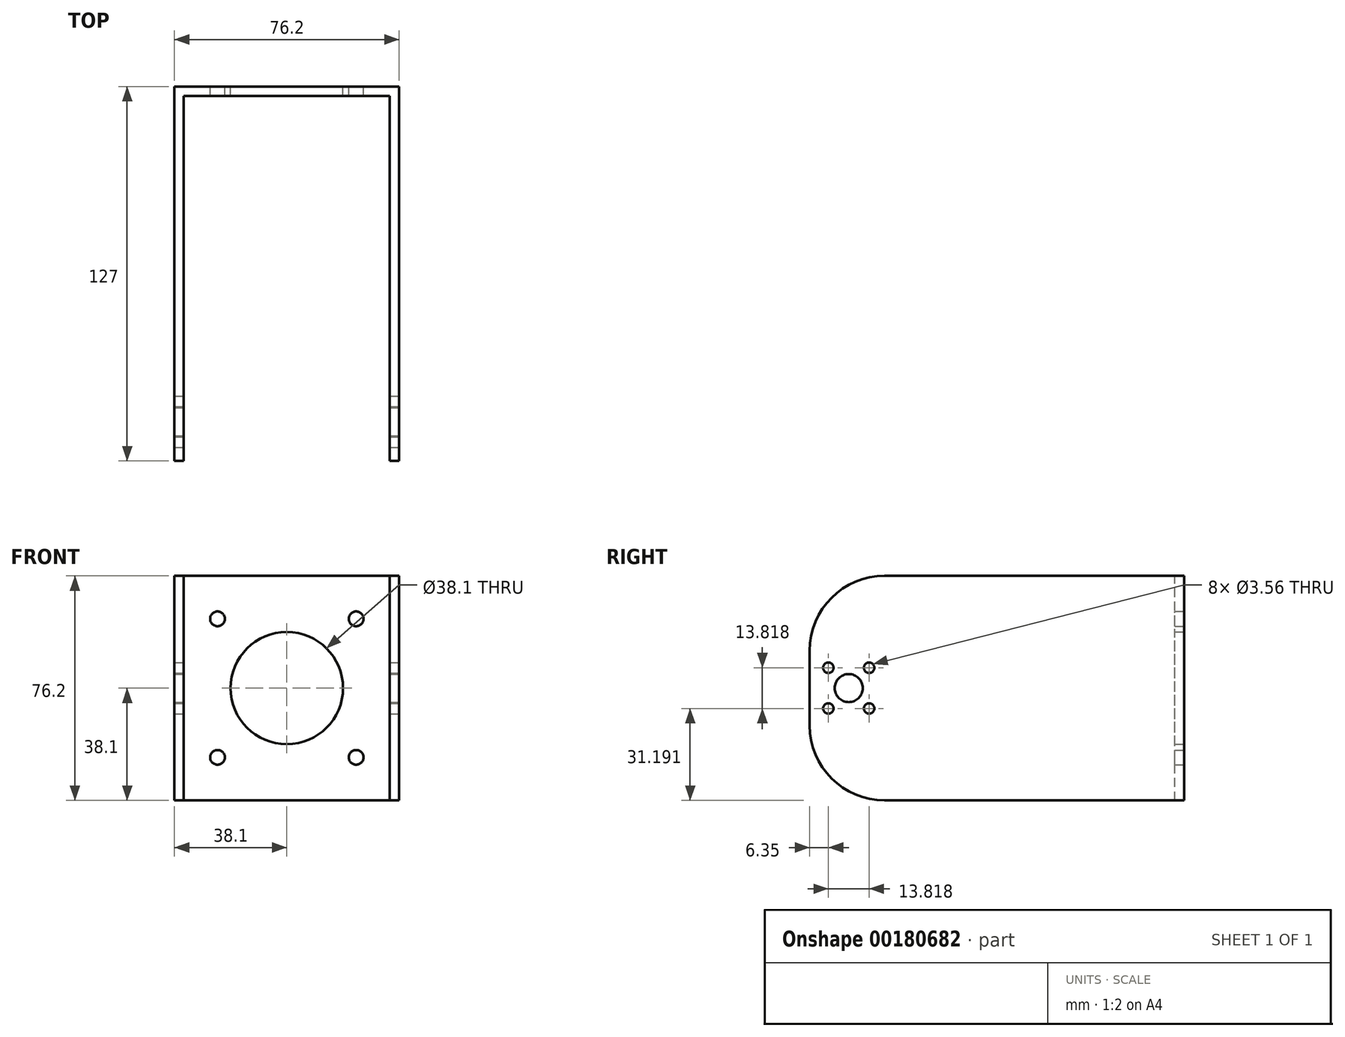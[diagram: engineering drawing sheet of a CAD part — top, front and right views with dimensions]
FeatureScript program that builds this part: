
annotation { "Feature Type Name" : "Feature", "Feature Type Description" : "" }
export const myFeature = defineFeature(function(context is Context, id is Id, definition is map)
    precondition{}
    {
        {
            var Q0;
            Q0=qCreatedBy(makeId("Front.planeOp"),FACE);
            var sketch = newSketch(context, id + "F0", { "sketchPlane" : qUnion([Q0])});
            skLineSegment(sketch, "E0.bottom", {"start": v(38.1, -38.1) * mm, "end": v(-38.1, -38.1) * mm});
            skLineSegment(sketch, "E0.top", {"start": v(38.1, 38.1) * mm, "end": v(-38.1, 38.1) * mm});
            skLineSegment(sketch, "E0.left", {"start": v(38.1, -38.1) * mm, "end": v(38.1, 38.1) * mm});
            skLineSegment(sketch, "E0.right", {"start": v(-38.1, -38.1) * mm, "end": v(-38.1, 38.1) * mm});
            skPoint(sketch, "E0.middle", {"position": v(0, 0) * mm});
            skLineSegment(sketch, "E1", {"start": v(-34.93, 38.1) * mm, "end": v(-34.93, -38.1) * mm});
            skLineSegment(sketch, "E2", {"start": v(-34.92, -38.1) * mm, "end": v(34.92, -38.1) * mm});
            skLineSegment(sketch, "E3", {"start": v(34.92, -38.1) * mm, "end": v(34.92, 38.1) * mm});
            skCircle(sketch, "E4", {"center": v(0, 0) * mm, "radius": 19.05 * mm});
            skCircle(sketch, "E5", {"center": v(-23.5, 23.5) * mm, "radius": 2.5 * mm});
            skCircle(sketch, "E6.0.1.0", {"center": v(-23.5, -23.5) * mm, "radius": 2.5 * mm});
            skCircle(sketch, "E6.1.0.0", {"center": v(23.5, 23.5) * mm, "radius": 2.5 * mm});
            skCircle(sketch, "E6.1.1.0", {"center": v(23.5, -23.5) * mm, "radius": 2.5 * mm});
            skLineSegment(sketch, "E6.direction1", {"start": v(-23.5, 23.5) * mm, "end": v(23.5, 23.5) * mm, "construction": true});
            skLineSegment(sketch, "E6.direction2", {"start": v(-23.5, 23.5) * mm, "end": v(-23.5, -23.5) * mm, "construction": true});
            skSolve(sketch);
        }
        {
            var Q0;
            {var subQ1=sQuery(id+"F0.wireOp",EDGE,"E1");Q0=makeQuery(id+"F0.imprint","IMPRINT",FACE,{"disambiguationData":[TD([[makeQuery(id+"F0.imprint","IMPRINT",EDGE,{"derivedFrom":subQ1}),1.0]])]});}
            extrude(context, id + "F1", {"entities" : qUnion([Q0]), "depth" : 3.17 * mm});
        }
        {
            var Q0;
            {var subQ0=sQuery(id+"F0.wireOp",EDGE,"E0.right");Q0=makeQuery(id+"F0.imprint","IMPRINT",FACE,{"disambiguationData":[TD([[makeQuery(id+"F0.imprint","IMPRINT",EDGE,{"derivedFrom":subQ0}),-1.0]])]});}
            var Q1;
            {var subQ0=sQuery(id+"F0.wireOp",EDGE,"E0.left");Q1=makeQuery(id+"F0.imprint","IMPRINT",FACE,{"disambiguationData":[TD([[makeQuery(id+"F0.imprint","IMPRINT",EDGE,{"derivedFrom":subQ0}),1.0]])]});}
            extrude(context, id + "F2", {"entities" : qUnion([Q0, Q1]), "operationType" : NewBodyOperationType.ADD, "depth" : 127 * mm});
        }
        {
            var Q0;
            Q0=makeQuery(id+"F2.opExtrude","SWEPT_FACE",FACE,{"disambiguationData":[OSD([sQuery(id+"F0.wireOp",EDGE,"E0.left")])]});
            var sketch = newSketch(context, id + "F3", { "sketchPlane" : qUnion([Q0])});
            skCircle(sketch, "E7", {"center": v(-113.74, 0) * mm, "radius": 4.76 * mm});
            skCircle(sketch, "E8", {"center": v(-120.65, 6.9) * mm, "radius": 1.78 * mm});
            skCircle(sketch, "E9.0.1.0", {"center": v(-120.65, -6.9) * mm, "radius": 1.78 * mm});
            skCircle(sketch, "E9.1.0.0", {"center": v(-106.83, 6.9) * mm, "radius": 1.78 * mm});
            skCircle(sketch, "E9.1.1.0", {"center": v(-106.83, -6.9) * mm, "radius": 1.78 * mm});
            skLineSegment(sketch, "E9.direction1", {"start": v(-120.65, 6.9) * mm, "end": v(-106.83, 6.9) * mm, "construction": true});
            skLineSegment(sketch, "E9.direction2", {"start": v(-120.65, 6.9) * mm, "end": v(-120.65, -6.9) * mm, "construction": true});
            skSolve(sketch);
        }
        {
            var Q0;
            Q0=makeQuery(id+"F3.imprint","IMPRINT",FACE,{"disambiguationData":[TD([[makeQuery(id+"F3.imprint","IMPRINT",EDGE,{"derivedFrom":sQuery(id+"F3.wireOp",EDGE,"E8")}),1.0]])]});
            var Q1;
            Q1=makeQuery(id+"F3.imprint","IMPRINT",FACE,{"disambiguationData":[TD([[makeQuery(id+"F3.imprint","IMPRINT",EDGE,{"derivedFrom":sQuery(id+"F3.wireOp",EDGE,"E9.1.0.0")}),1.0]])]});
            var Q2;
            Q2=makeQuery(id+"F3.imprint","IMPRINT",FACE,{"disambiguationData":[TD([[makeQuery(id+"F3.imprint","IMPRINT",EDGE,{"derivedFrom":sQuery(id+"F3.wireOp",EDGE,"E9.1.1.0")}),1.0]])]});
            var Q3;
            Q3=makeQuery(id+"F3.imprint","IMPRINT",FACE,{"disambiguationData":[TD([[makeQuery(id+"F3.imprint","IMPRINT",EDGE,{"derivedFrom":sQuery(id+"F3.wireOp",EDGE,"E9.0.1.0")}),1.0]])]});
            var Q4;
            Q4=makeQuery(id+"F3.imprint","IMPRINT",FACE,{"disambiguationData":[TD([[makeQuery(id+"F3.imprint","IMPRINT",EDGE,{"derivedFrom":sQuery(id+"F3.wireOp",EDGE,"E7")}),1.0]])]});
            extrude(context, id + "F4", {"entities" : qUnion([Q0, Q1, Q2, Q3, Q4]), "operationType" : NewBodyOperationType.REMOVE, "endBound" : BoundingType.THROUGH_ALL, "oppositeDirection" : true, "depth" : 25.4 * mm});
        }
        {
            var Q0;
            {var subQ0=sQuery(id+"F0.wireOp",EDGE,"E0.top");Q0=makeQuery(id+"F2.opExtrude","CAP_EDGE",EDGE,{"disambiguationData":[OSD([subQ0]),TDD([makeQuery(id+"F0.imprint","IMPRINT",EDGE,{"disambiguationData":[TD([[makeQuery(id+"F0.imprint","INTERSECT",VERTEX,{"derivedFrom":[subQ0,sQuery(id+"F0.wireOp",EDGE,"E0.left")]}),-1.0]])],"derivedFrom":subQ0})])],"isStart":false});}
            fillet(context, id + "F5", {"entities" : qUnion([Q0]), "radius" : 25.4 * mm, "tangentPropagation" : true, "allowEdgeOverflow" : false});
        }
        {
            var Q0;
            {var subQ0=sQuery(id+"F0.wireOp",EDGE,"E0.top");Q0=makeQuery(id+"F2.opExtrude","CAP_EDGE",EDGE,{"disambiguationData":[OSD([subQ0]),TDD([makeQuery(id+"F0.imprint","IMPRINT",EDGE,{"disambiguationData":[TD([[makeQuery(id+"F0.imprint","INTERSECT",VERTEX,{"derivedFrom":[subQ0,sQuery(id+"F0.wireOp",EDGE,"E0.right")]}),1.0]])],"derivedFrom":subQ0})])],"isStart":false});}
            fillet(context, id + "F6", {"entities" : qUnion([Q0]), "radius" : 25.4 * mm, "tangentPropagation" : true, "allowEdgeOverflow" : false});
        }
        {
            var Q0;
            {var subQ0=sQuery(id+"F0.wireOp",EDGE,"E0.bottom");Q0=makeQuery(id+"F2.opExtrude","CAP_EDGE",EDGE,{"disambiguationData":[OSD([subQ0]),TDD([makeQuery(id+"F0.imprint","IMPRINT",EDGE,{"disambiguationData":[TD([[makeQuery(id+"F0.imprint","INTERSECT",VERTEX,{"derivedFrom":[subQ0,sQuery(id+"F0.wireOp",EDGE,"E0.right")]}),1.0]])],"derivedFrom":subQ0})])],"isStart":false});}
            fillet(context, id + "F7", {"entities" : qUnion([Q0]), "radius" : 25.4 * mm, "tangentPropagation" : true, "allowEdgeOverflow" : false});
        }
        {
            var Q0;
            {var subQ0=sQuery(id+"F0.wireOp",EDGE,"E0.bottom");Q0=makeQuery(id+"F2.opExtrude","CAP_EDGE",EDGE,{"disambiguationData":[OSD([subQ0]),TDD([makeQuery(id+"F0.imprint","IMPRINT",EDGE,{"disambiguationData":[TD([[makeQuery(id+"F0.imprint","INTERSECT",VERTEX,{"derivedFrom":[subQ0,sQuery(id+"F0.wireOp",EDGE,"E0.left")]}),-1.0]])],"derivedFrom":subQ0})])],"isStart":false});}
            fillet(context, id + "F8", {"entities" : qUnion([Q0]), "radius" : 25.4 * mm, "tangentPropagation" : true, "allowEdgeOverflow" : false});
        }
    });
